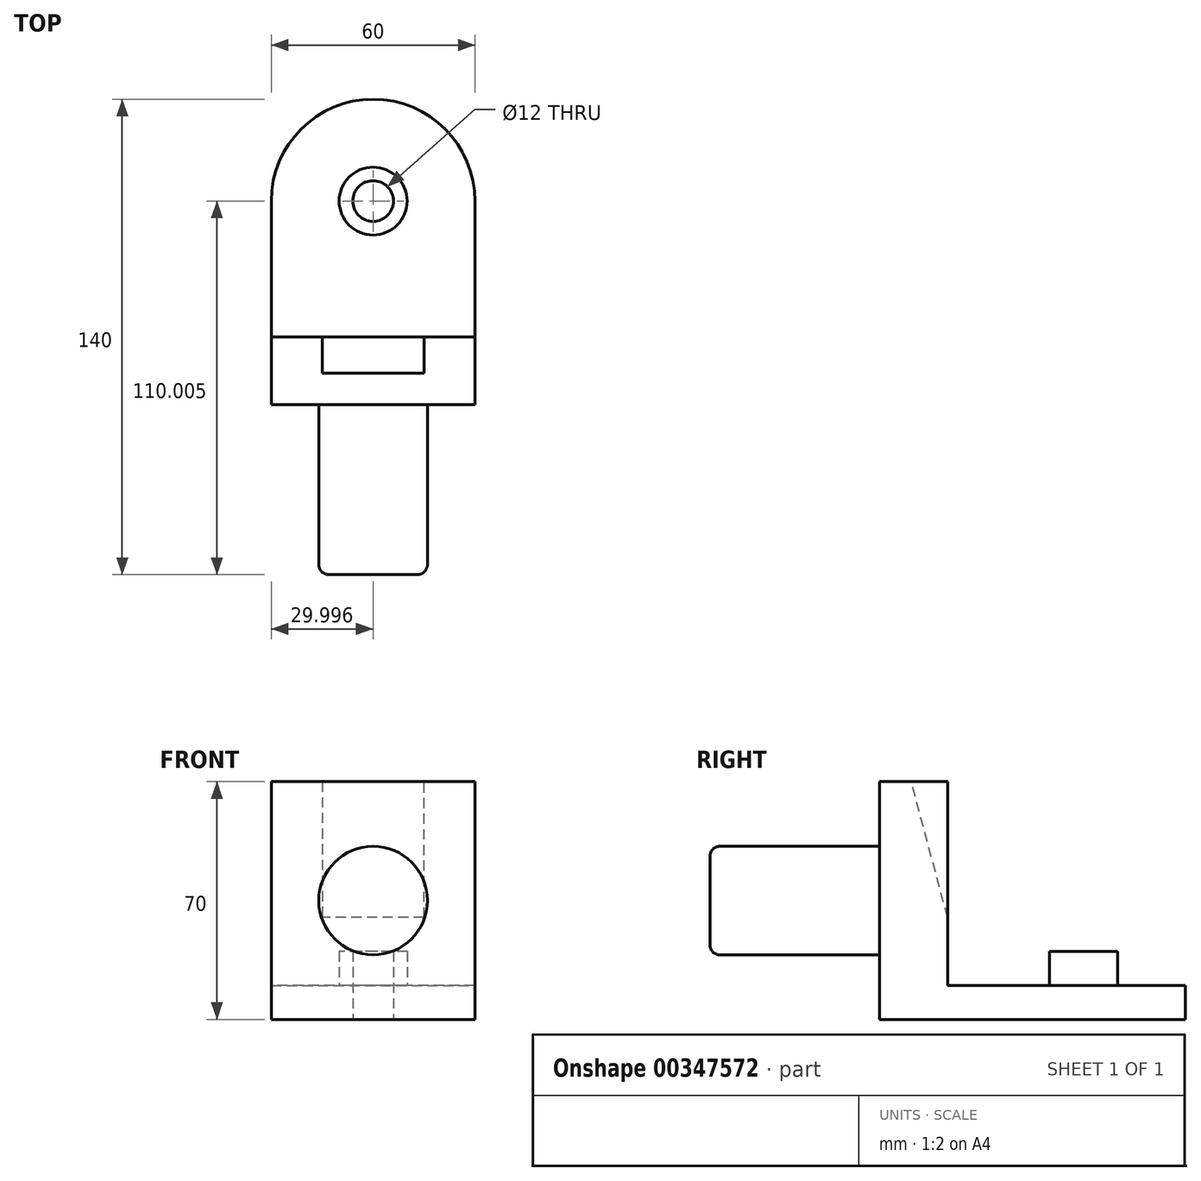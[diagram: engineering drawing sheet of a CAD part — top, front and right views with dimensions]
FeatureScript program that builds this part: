
annotation { "Feature Type Name" : "Feature", "Feature Type Description" : "" }
export const myFeature = defineFeature(function(context is Context, id is Id, definition is map)
    precondition{}
    {
        {
            var Q0;
            Q0=qCreatedBy(makeId("Top.planeOp"),FACE);
            var sketch = newSketch(context, id + "F0", { "sketchPlane" : qUnion([Q0])});
            skLineSegment(sketch, "E0", {"start": v(-35.56, 30.88) * mm, "end": v(-35.56, -9.12) * mm});
            skLineSegment(sketch, "E1", {"start": v(-35.56, -9.12) * mm, "end": v(24.44, -9.12) * mm});
            skLineSegment(sketch, "E2", {"start": v(24.44, -9.12) * mm, "end": v(24.44, 30.88) * mm});
            skLineSegment(sketch, "E3", {"start": v(-5.56, 60.88) * mm, "end": v(-5.56, 60.88) * mm});
            skPoint(sketch, "E4.visualSharp", {"position": v(-35.56, 60.88) * mm});
            skArc(sketch, "E4.filletArc", {"start": v(-5.56, 60.88) * mm, "mid": v(-26.78, 52.1) * mm, "end": v(-35.56, 30.88) * mm});
            skArc(sketch, "E5.filletArc", {"start": v(24.44, 30.88) * mm, "mid": v(15.65, 52.1) * mm, "end": v(-5.56, 60.88) * mm});
            skLineSegment(sketch, "E6", {"start": v(-35.56, -9.12) * mm, "end": v(-35.56, -29.12) * mm});
            skLineSegment(sketch, "E7", {"start": v(-35.56, -29.12) * mm, "end": v(24.44, -29.12) * mm});
            skLineSegment(sketch, "E8", {"start": v(24.44, -29.12) * mm, "end": v(24.44, -9.12) * mm});
            skPoint(sketch, "E9.visualSharp", {"position": v(-15.56, -79.12) * mm});
            skPoint(sketch, "E10.visualSharp", {"position": v(5.9, -79.12) * mm});
            skPoint(sketch, "E11.orphan", {"position": v(-15.56, -29.12) * mm});
            skPoint(sketch, "E12.start.orphan", {"position": v(5.9, -29.12) * mm});
            skCircle(sketch, "E13", {"center": v(-5.56, 30.88) * mm, "radius": 6 * mm});
            skCircle(sketch, "E14", {"center": v(-5.56, 30.88) * mm, "radius": 10 * mm});
            skSolve(sketch);
        }
        {
            var Q0;
            Q0=makeQuery(id+"F0.imprint","IMPRINT",FACE,{"disambiguationData":[TD([[makeQuery(id+"F0.imprint","IMPRINT",EDGE,{"derivedFrom":sQuery(id+"F0.wireOp",EDGE,"E0")}),1.0]])]});
            extrude(context, id + "F1", {"entities" : qUnion([Q0]), "depth" : 10 * mm});
        }
        {
            var Q0;
            Q0=makeQuery(id+"F0.imprint","IMPRINT",FACE,{"disambiguationData":[TD([[makeQuery(id+"F0.imprint","IMPRINT",EDGE,{"derivedFrom":sQuery(id+"F0.wireOp",EDGE,"E13")}),-1.0]])]});
            extrude(context, id + "F2", {"entities" : qUnion([Q0]), "operationType" : NewBodyOperationType.ADD, "depth" : 20 * mm});
        }
        {
            var Q0;
            Q0=makeQuery(id+"F0.imprint","IMPRINT",FACE,{"disambiguationData":[TD([[makeQuery(id+"F0.imprint","IMPRINT",EDGE,{"derivedFrom":sQuery(id+"F0.wireOp",EDGE,"E1")}),-1.0]])]});
            extrude(context, id + "F3", {"entities" : qUnion([Q0]), "operationType" : NewBodyOperationType.ADD, "depth" : 70 * mm});
        }
        {
            var Q0;
            Q0=makeQuery(id+"F3.opExtrude","SWEPT_FACE",FACE,{"disambiguationData":[OSD([sQuery(id+"F0.wireOp",EDGE,"E7")])]});
            var sketch = newSketch(context, id + "F4", { "sketchPlane" : qUnion([Q0])});
            skPoint(sketch, "E15.start.orphan", {"position": v(-35.56, 35) * mm});
            skCircle(sketch, "E16", {"center": v(-5.56, 35) * mm, "radius": 16 * mm});
            skPoint(sketch, "E17.orphan", {"position": v(-5.56, 0) * mm});
            skSolve(sketch);
        }
        {
            var Q0;
            Q0=makeQuery(id+"F4.imprint","IMPRINT",FACE,{"disambiguationData":[TD([[makeQuery(id+"F4.imprint","IMPRINT",EDGE,{"derivedFrom":sQuery(id+"F4.wireOp",EDGE,"E16")}),1.0]])]});
            extrude(context, id + "F5", {"entities" : qUnion([Q0]), "operationType" : NewBodyOperationType.ADD, "depth" : 50 * mm});
        }
        {
            var Q0;
            Q0=makeQuery(id+"F5.opExtrude","CAP_EDGE",EDGE,{"disambiguationData":[OSD([sQuery(id+"F4.wireOp",EDGE,"E16")])],"isStart":false});
            fillet(context, id + "F6", {"entities" : qUnion([Q0]), "radius" : 3 * mm, "tangentPropagation" : true, "allowEdgeOverflow" : false});
        }
        {
            var Q0;
            Q0=makeQuery(id+"F3.boolean.opBoolean","MERGE",FACE,{"derivedFrom":[makeQuery(id+"F1.opExtrude","SWEPT_FACE",FACE,{"disambiguationData":[OSD([sQuery(id+"F0.wireOp",EDGE,"E2")])]}),makeQuery(id+"F3.opExtrude","SWEPT_FACE",FACE,{"disambiguationData":[OSD([sQuery(id+"F0.wireOp",EDGE,"E8")])]})]});
            var sketch = newSketch(context, id + "F7", { "sketchPlane" : qUnion([Q0])});
            skLineSegment(sketch, "E18", {"start": v(-9.12, 70) * mm, "end": v(-9.12, 30) * mm});
            skLineSegment(sketch, "E19", {"start": v(-9.12, 30) * mm, "end": v(-19.83, 70) * mm});
            skSolve(sketch);
        }
        {
            var Q0;
            Q0=makeQuery(id+"F3.boolean.opBoolean","MERGE",FACE,{"derivedFrom":[makeQuery(id+"F1.opExtrude","SWEPT_FACE",FACE,{"disambiguationData":[OSD([sQuery(id+"F0.wireOp",EDGE,"E0")])]}),makeQuery(id+"F3.opExtrude","SWEPT_FACE",FACE,{"disambiguationData":[OSD([sQuery(id+"F0.wireOp",EDGE,"E6")])]})]});
            var sketch = newSketch(context, id + "F8", { "sketchPlane" : qUnion([Q0])});
            skLineSegment(sketch, "E20", {"start": v(9.12, 70) * mm, "end": v(9.12, 30) * mm});
            skLineSegment(sketch, "E21", {"start": v(9.12, 30) * mm, "end": v(19.83, 70) * mm});
            skSolve(sketch);
        }
        {
            var Q0;
            {var subQ0=sQuery(id+"F8.wireOp",EDGE,"E20");Q0=makeQuery(id+"F8.imprint","IMPRINT",FACE,{"disambiguationData":[TD([[makeQuery(id+"F8.imprint","IMPRINT",EDGE,{"derivedFrom":subQ0}),1.0]])]});}
            extrude(context, id + "F9", {"entities" : qUnion([Q0]), "operationType" : NewBodyOperationType.REMOVE, "oppositeDirection" : true, "depth" : 77.2 * mm});
        }
        {
            var Q0;
            {var subQ0=sQuery(id+"F8.wireOp",EDGE,"E20");Q0=makeQuery(id+"F8.imprint","IMPRINT",FACE,{"disambiguationData":[TD([[makeQuery(id+"F8.imprint","IMPRINT",EDGE,{"derivedFrom":subQ0}),1.0]])]});}
            var Q1;
            {var subQ4=sQuery(id+"F8.wireOp",EDGE,"E21");Q1=makeQuery(id+"F8.imprint","IMPRINT",FACE,{"disambiguationData":[TD([[makeQuery(id+"F8.imprint","IMPRINT",EDGE,{"derivedFrom":subQ4}),-1.0]])]});}
            extrude(context, id + "F10", {"entities" : qUnion([Q0, Q1]), "operationType" : NewBodyOperationType.ADD, "oppositeDirection" : true, "depth" : 15 * mm});
        }
        {
            var Q0;
            {var subQ4=sQuery(id+"F7.wireOp",EDGE,"E19");Q0=makeQuery(id+"F7.imprint","IMPRINT",FACE,{"disambiguationData":[TD([[makeQuery(id+"F7.imprint","IMPRINT",EDGE,{"derivedFrom":subQ4}),1.0]])]});}
            var Q1;
            {var subQ0=sQuery(id+"F7.wireOp",EDGE,"E18");Q1=makeQuery(id+"F7.imprint","IMPRINT",FACE,{"disambiguationData":[TD([[makeQuery(id+"F7.imprint","IMPRINT",EDGE,{"derivedFrom":subQ0}),-1.0]])]});}
            extrude(context, id + "F11", {"entities" : qUnion([Q0, Q1]), "operationType" : NewBodyOperationType.ADD, "oppositeDirection" : true, "depth" : 15 * mm});
        }
    });
